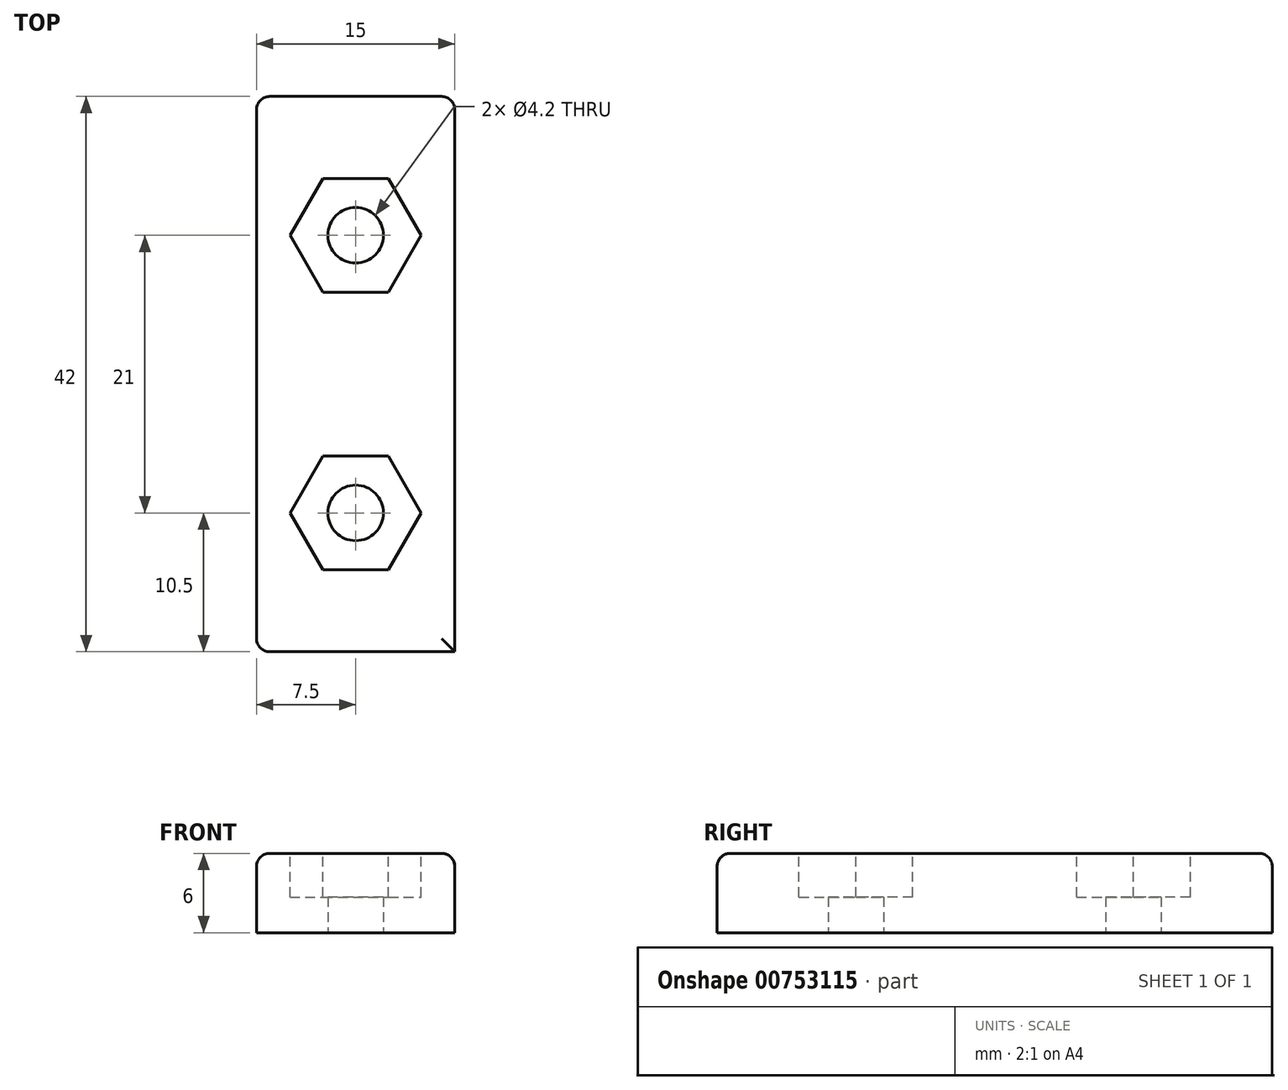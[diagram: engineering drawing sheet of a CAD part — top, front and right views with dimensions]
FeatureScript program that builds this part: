
annotation { "Feature Type Name" : "Feature", "Feature Type Description" : "" }
export const myFeature = defineFeature(function(context is Context, id is Id, definition is map)
    precondition{}
    {
        {
            var Q0;
            Q0=qCreatedBy(makeId("Top.planeOp"),FACE);
            var sketch = newSketch(context, id + "F0", { "sketchPlane" : qUnion([Q0])});
            skLineSegment(sketch, "E0.bottom", {"start": v(7.5, 21) * mm, "end": v(-7.5, 21) * mm});
            skLineSegment(sketch, "E0.top", {"start": v(7.5, -21) * mm, "end": v(-7.5, -21) * mm});
            skLineSegment(sketch, "E0.left", {"start": v(7.5, 21) * mm, "end": v(7.5, -21) * mm});
            skLineSegment(sketch, "E0.right", {"start": v(-7.5, 21) * mm, "end": v(-7.5, -21) * mm});
            skPoint(sketch, "E0.middle", {"position": v(0, 0) * mm});
            skLineSegment(sketch, "E1", {"start": v(-23.2, 0) * mm, "end": v(33.16, 0) * mm, "construction": true});
            skPoint(sketch, "E1.endSnap0", {"position": v(7.5, 0) * mm});
            skLineSegment(sketch, "E2", {"start": v(0, 0) * mm, "end": v(0, 21) * mm, "construction": true});
            skCircle(sketch, "E3", {"center": v(0, -10.5) * mm, "radius": 2.1 * mm});
            skCircle(sketch, "E4", {"center": v(0, 10.5) * mm, "radius": 2.1 * mm});
            skSolve(sketch);
        }
        {
            var Q0;
            Q0=makeQuery(id+"F0.imprint","IMPRINT",FACE,{"disambiguationData":[TD([[makeQuery(id+"F0.imprint","IMPRINT",EDGE,{"derivedFrom":sQuery(id+"F0.wireOp",EDGE,"E0.bottom")}),1.0]])]});
            var Q1;
            Q1=makeQuery(id+"F0.imprint","IMPRINT",FACE,{"disambiguationData":[TD([[makeQuery(id+"F0.imprint","IMPRINT",EDGE,{"derivedFrom":sQuery(id+"F0.wireOp",EDGE,"e398b884-3d2a-4632-9d2e-87e8c9457e84.0")}),-1.0]])]});
            var Q2;
            Q2=makeQuery(id+"F0.imprint","IMPRINT",FACE,{"disambiguationData":[TD([[makeQuery(id+"F0.imprint","IMPRINT",EDGE,{"derivedFrom":sQuery(id+"F0.wireOp",EDGE,"E3")}),1.0]])]});
            var Q3;
            Q3=makeQuery(id+"F0.imprint","IMPRINT",FACE,{"disambiguationData":[TD([[makeQuery(id+"F0.imprint","IMPRINT",EDGE,{"derivedFrom":sQuery(id+"F0.wireOp",EDGE,"cb06f1ee-6506-41bb-9003-6ed66bc601ca0.MirrorCS")}),1.0]])]});
            var Q4;
            Q4=makeQuery(id+"F0.imprint","IMPRINT",FACE,{"disambiguationData":[TD([[makeQuery(id+"F0.imprint","IMPRINT",EDGE,{"derivedFrom":sQuery(id+"F0.wireOp",EDGE,"E4")}),1.0]])]});
            extrude(context, id + "F1", {"entities" : qUnion([Q0, Q1, Q2, Q3, Q4]), "depth" : 6 * mm, "offsetDistance" : 25 * mm});
        }
        {
            var Q0;
            Q0=makeQuery(id+"F0.imprint","IMPRINT",FACE,{"disambiguationData":[TD([[makeQuery(id+"F0.imprint","IMPRINT",EDGE,{"derivedFrom":sQuery(id+"F0.wireOp",EDGE,"E4")}),1.0]])]});
            var Q1;
            Q1=makeQuery(id+"F0.imprint","IMPRINT",FACE,{"disambiguationData":[TD([[makeQuery(id+"F0.imprint","IMPRINT",EDGE,{"derivedFrom":sQuery(id+"F0.wireOp",EDGE,"E3")}),1.0]])]});
            var Q2;
            Q2=sQuery(id+"F0.wireOp",EDGE,"E4");
            var Q3;
            Q3=sQuery(id+"F0.wireOp",EDGE,"E3");
            extrude(context, id + "F2", {"entities" : qUnion([Q0, Q1]), "operationType" : NewBodyOperationType.REMOVE, "surfaceEntities" : qUnion([Q2, Q3]), "endBound" : BoundingType.THROUGH_ALL, "depth" : 25 * mm, "offsetDistance" : 25 * mm});
        }
        {
            var Q0;
            Q0=makeQuery(id+"F1.opExtrude","CAP_FACE",FACE,{"disambiguationData":[OSD([sQuery(id+"F0.wireOp",EDGE,"E0.bottom"),sQuery(id+"F0.wireOp",EDGE,"E0.top"),sQuery(id+"F0.wireOp",EDGE,"E0.left"),sQuery(id+"F0.wireOp",EDGE,"E0.right")])],"isStart":false});
            var sketch = newSketch(context, id + "F3", { "sketchPlane" : qUnion([Q0])});
            skCircle(sketch, "E5.cCircle", {"center": v(0, 10.5) * mm, "radius": 4.3 * mm, "construction": true});
            skLineSegment(sketch, "E5.0", {"start": v(2.48, 14.8) * mm, "end": v(4.97, 10.5) * mm});
            skLineSegment(sketch, "E5.1", {"start": v(4.97, 10.5) * mm, "end": v(2.48, 6.2) * mm});
            skLineSegment(sketch, "E5.2", {"start": v(2.48, 6.2) * mm, "end": v(-2.48, 6.2) * mm});
            skLineSegment(sketch, "E5.3", {"start": v(-2.48, 6.2) * mm, "end": v(-4.97, 10.5) * mm});
            skLineSegment(sketch, "E5.4", {"start": v(-4.97, 10.5) * mm, "end": v(-2.48, 14.8) * mm});
            skLineSegment(sketch, "E5.5", {"start": v(-2.48, 14.8) * mm, "end": v(2.48, 14.8) * mm});
            skPoint(sketch, "E5.0.midPoint", {"position": v(3.72, 12.65) * mm});
            skCircle(sketch, "E6.cCircle", {"center": v(0, -10.5) * mm, "radius": 4.3 * mm, "construction": true});
            skLineSegment(sketch, "E6.0", {"start": v(2.48, -6.2) * mm, "end": v(4.97, -10.5) * mm});
            skLineSegment(sketch, "E6.1", {"start": v(4.97, -10.5) * mm, "end": v(2.48, -14.8) * mm});
            skLineSegment(sketch, "E6.2", {"start": v(2.48, -14.8) * mm, "end": v(-2.48, -14.8) * mm});
            skLineSegment(sketch, "E6.3", {"start": v(-2.48, -14.8) * mm, "end": v(-4.97, -10.5) * mm});
            skLineSegment(sketch, "E6.4", {"start": v(-4.97, -10.5) * mm, "end": v(-2.48, -6.2) * mm});
            skLineSegment(sketch, "E6.5", {"start": v(-2.48, -6.2) * mm, "end": v(2.48, -6.2) * mm});
            skPoint(sketch, "E6.0.midPoint", {"position": v(3.72, -8.35) * mm});
            skSolve(sketch);
        }
        {
            var Q0;
            Q0=makeQuery(id+"F3.imprint","IMPRINT",FACE,{"disambiguationData":[TD([[makeQuery(id+"F3.imprint","IMPRINT",EDGE,{"derivedFrom":sQuery(id+"F3.wireOp",EDGE,"E6.0")}),-1.0]])]});
            var Q1;
            Q1=makeQuery(id+"F3.imprint","IMPRINT",FACE,{"disambiguationData":[TD([[makeQuery(id+"F3.imprint","IMPRINT",EDGE,{"derivedFrom":sQuery(id+"F3.wireOp",EDGE,"E5.0")}),-1.0]])]});
            var Q2;
            Q2=sQuery(id+"F3.wireOp",EDGE,"E5.2");
            var Q3;
            Q3=sQuery(id+"F3.wireOp",EDGE,"E5.1");
            var Q4;
            Q4=sQuery(id+"F3.wireOp",EDGE,"E5.0");
            var Q5;
            Q5=sQuery(id+"F3.wireOp",EDGE,"E5.5");
            var Q6;
            Q6=sQuery(id+"F3.wireOp",EDGE,"E5.4");
            var Q7;
            Q7=sQuery(id+"F3.wireOp",EDGE,"E5.3");
            var Q8;
            Q8=sQuery(id+"F3.wireOp",EDGE,"E6.5");
            var Q9;
            Q9=sQuery(id+"F3.wireOp",EDGE,"E6.4");
            var Q10;
            Q10=sQuery(id+"F3.wireOp",EDGE,"E6.3");
            var Q11;
            Q11=sQuery(id+"F3.wireOp",EDGE,"E6.2");
            var Q12;
            Q12=sQuery(id+"F3.wireOp",EDGE,"E6.1");
            var Q13;
            Q13=sQuery(id+"F3.wireOp",EDGE,"E6.0");
            extrude(context, id + "F4", {"entities" : qUnion([Q0, Q1]), "operationType" : NewBodyOperationType.REMOVE, "surfaceEntities" : qUnion([Q2, Q3, Q4, Q5, Q6, Q7, Q8, Q9, Q10, Q11, Q12, Q13]), "oppositeDirection" : true, "depth" : 3.3 * mm, "offsetDistance" : 25 * mm});
        }
        {
            var Q0;
            Q0=makeQuery(id+"F1.opExtrude","SWEPT_EDGE",EDGE,{"disambiguationData":[OSD([sQuery(id+"F0.wireOp",EDGE,"E0.bottom"),sQuery(id+"F0.wireOp",EDGE,"E0.right")])]});
            var Q1;
            Q1=makeQuery(id+"F1.opExtrude","SWEPT_EDGE",EDGE,{"disambiguationData":[OSD([sQuery(id+"F0.wireOp",EDGE,"E0.top"),sQuery(id+"F0.wireOp",EDGE,"E0.right")])]});
            var Q2;
            Q2=makeQuery(id+"F1.opExtrude","CAP_EDGE",EDGE,{"disambiguationData":[OSD([sQuery(id+"F0.wireOp",EDGE,"E0.top")])],"isStart":false});
            var Q3;
            Q3=makeQuery(id+"F1.opExtrude","CAP_EDGE",EDGE,{"disambiguationData":[OSD([sQuery(id+"F0.wireOp",EDGE,"E0.right")])],"isStart":false});
            var Q4;
            Q4=makeQuery(id+"F1.opExtrude","CAP_EDGE",EDGE,{"disambiguationData":[OSD([sQuery(id+"F0.wireOp",EDGE,"E0.bottom")])],"isStart":false});
            var Q5;
            Q5=makeQuery(id+"F1.opExtrude","CAP_EDGE",EDGE,{"disambiguationData":[OSD([sQuery(id+"F0.wireOp",EDGE,"E0.left")])],"isStart":false});
            var Q6;
            Q6=makeQuery(id+"F1.opExtrude","SWEPT_EDGE",EDGE,{"disambiguationData":[OSD([sQuery(id+"F0.wireOp",EDGE,"E0.bottom"),sQuery(id+"F0.wireOp",EDGE,"E0.left")])]});
            fillet(context, id + "F5", {"entities" : qUnion([Q0, Q1, Q2, Q3, Q4, Q5, Q6]), "radius" : 1 * mm, "tangentPropagation" : true, "allowEdgeOverflow" : false});
        }
    });
